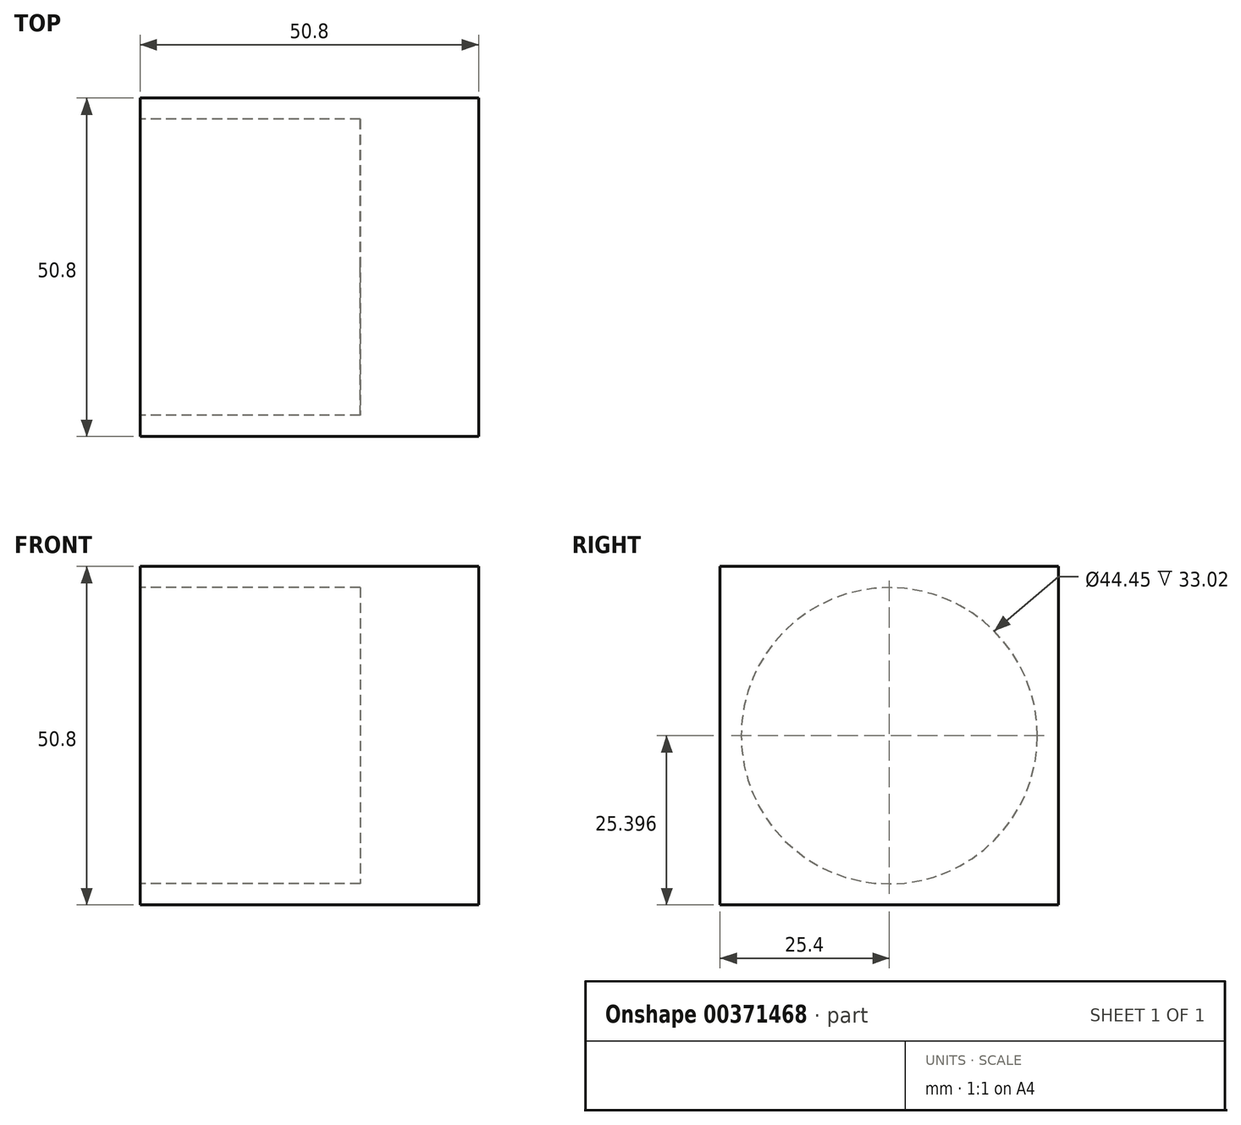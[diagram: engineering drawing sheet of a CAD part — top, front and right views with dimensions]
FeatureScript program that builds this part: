
annotation { "Feature Type Name" : "Feature", "Feature Type Description" : "" }
export const myFeature = defineFeature(function(context is Context, id is Id, definition is map)
    precondition{}
    {
        {
            var Q0;
            Q0=qCreatedBy(makeId("Front.planeOp"),FACE);
            var sketch = newSketch(context, id + "F0", { "sketchPlane" : qUnion([Q0])});
            skLineSegment(sketch, "E0.bottom", {"start": v(-33.35, 35.02) * mm, "end": v(17.45, 35.02) * mm});
            skLineSegment(sketch, "E0.top", {"start": v(-33.35, -15.78) * mm, "end": v(17.45, -15.78) * mm});
            skLineSegment(sketch, "E0.left", {"start": v(-33.35, 35.02) * mm, "end": v(-33.35, -15.78) * mm});
            skLineSegment(sketch, "E0.right", {"start": v(17.45, 35.02) * mm, "end": v(17.45, -15.78) * mm});
            skSolve(sketch);
        }
        {
            var Q0;
            Q0=makeQuery(id+"F0.imprint","IMPRINT",FACE,{"disambiguationData":[TD([[makeQuery(id+"F0.imprint","IMPRINT",EDGE,{"derivedFrom":sQuery(id+"F0.wireOp",EDGE,"E0.bottom")}),-1.0]])]});
            extrude(context, id + "F1", {"entities" : qUnion([Q0]), "depth" : 50.8 * mm});
        }
        {
            var Q0;
            Q0=makeQuery(id+"F1.opExtrude","SWEPT_FACE",FACE,{"disambiguationData":[OSD([sQuery(id+"F0.wireOp",EDGE,"E0.left")])]});
            var sketch = newSketch(context, id + "F2", { "sketchPlane" : qUnion([Q0])});
            skCircle(sketch, "E1", {"center": v(25.4, 9.62) * mm, "radius": 22.23 * mm});
            skPoint(sketch, "E1.centerSnap0", {"position": v(25.4, 35.02) * mm});
            skPoint(sketch, "E1.centerSnap1", {"position": v(0, 9.62) * mm});
            skLineSegment(sketch, "E2.bottom", {"start": v(-56.57, 28.2) * mm, "end": v(-5.77, 28.2) * mm});
            skLineSegment(sketch, "E2.top", {"start": v(-56.57, -22.6) * mm, "end": v(-5.77, -22.6) * mm});
            skLineSegment(sketch, "E2.left", {"start": v(-56.57, 28.2) * mm, "end": v(-56.57, -22.6) * mm});
            skLineSegment(sketch, "E2.right", {"start": v(-5.77, 28.2) * mm, "end": v(-5.77, -22.6) * mm});
            skCircle(sketch, "E3", {"center": v(-31.17, 2.8) * mm, "radius": 19.69 * mm});
            skPoint(sketch, "E3.centerSnap0", {"position": v(-56.57, 2.8) * mm});
            skPoint(sketch, "E3.centerSnap1", {"position": v(-31.17, 28.2) * mm});
            skSolve(sketch);
        }
        {
            var Q0;
            Q0=makeQuery(id+"F2.imprint","IMPRINT",FACE,{"disambiguationData":[TD([[makeQuery(id+"F2.imprint","IMPRINT",EDGE,{"derivedFrom":sQuery(id+"F2.wireOp",EDGE,"E1")}),1.0]])]});
            extrude(context, id + "F3", {"entities" : qUnion([Q0]), "operationType" : NewBodyOperationType.REMOVE, "oppositeDirection" : true, "depth" : 33.02 * mm});
        }
    });
